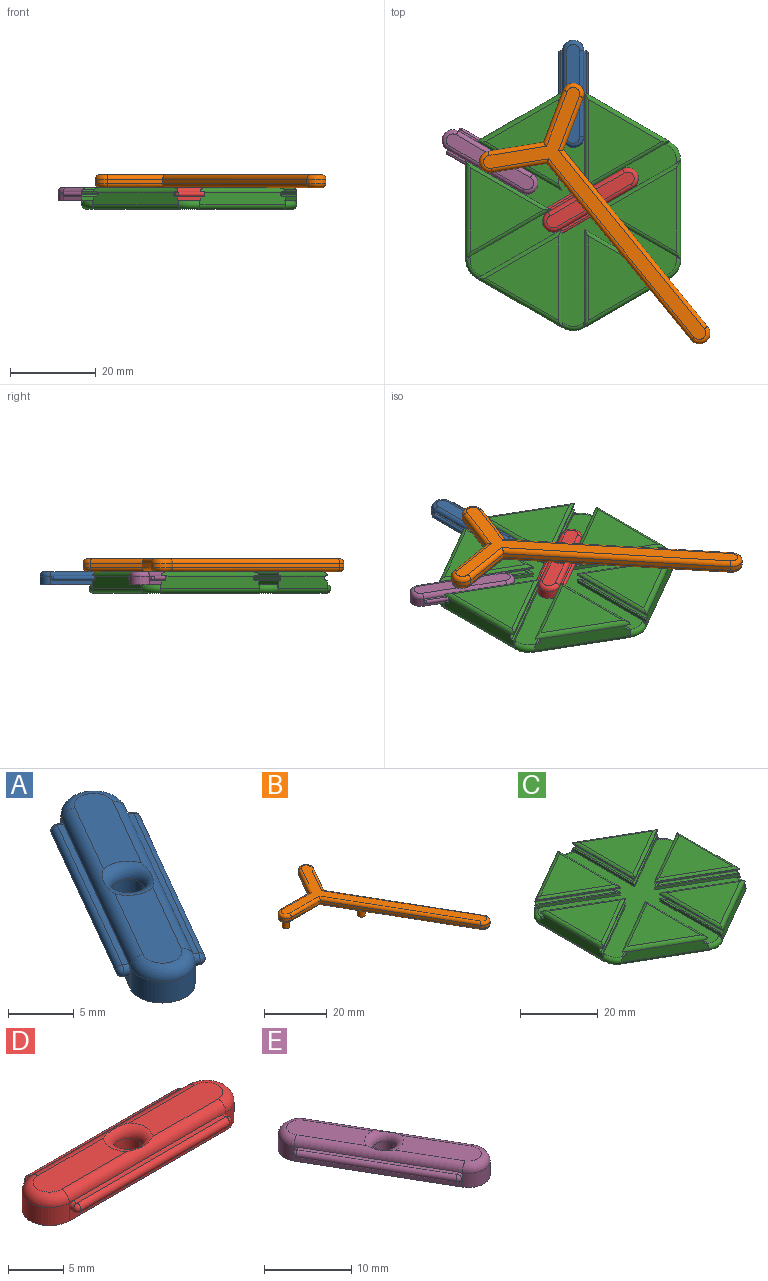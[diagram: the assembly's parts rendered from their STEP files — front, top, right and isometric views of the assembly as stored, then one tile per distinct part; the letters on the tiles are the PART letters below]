
ASSEMBLY  parts=5 mates=9
PART A: 27 faces, bbox 15.7x22.7x3 mm
  f0: plane 17.32x10mm, normal (0.87,-0.5,0), area 20.1mm2, adj f4,f5,f7,f16,f22,f25
  f1: plane 17.32x10mm, normal (-0.87,0.5,0), area 20.1mm2, adj f4,f5,f7,f14,f17,f19
  f2: plane 9.46x6.96mm, normal (0,0,1), area 27.3mm2, adj f8,f10,f11,f12
  f3: plane 9.46x6.96mm, normal (0,0,1), area 27.3mm2, adj f8,f9,f10,f12
  f4: cylinder r=2.5mm len=4.75mm, axis (0,0,-1), area 15.8mm2, adj f0,f1,f5,f8,f11,f12,f19,f25
  f5: plane 22.32x15mm, normal (0,0,-1), area 114.7mm2, adj f0,f1,f4,f6,f7
  f6: cylinder r=1.25mm len=2.5mm, axis (0,0,-1), area 15.7mm2, adj f5,f10
  f7: cylinder r=2.5mm len=4.75mm, axis (0,0,-1), area 15.8mm2, adj f0,f1,f5,f8,f9,f12,f17,f22
  f8: cylinder r=1mm len=17.82mm, axis (0.5,0.87,0), area 30.6mm2, adj f2,f3,f4,f7,f9,f10,f11,f13
  f9: torus R=1.5mm, axis (0,0,1), area 10.5mm2, adj f3,f7,f8,f12
  f10: torus R=2.25mm, axis (0,0,1), area 14.1mm2, adj f2,f3,f6,f8,f12
  f11: torus R=1.5mm, axis (0,0,1), area 10.5mm2, adj f2,f4,f8,f12
  f12: cylinder r=1mm len=17.82mm, axis (-0.5,-0.87,0), area 30.6mm2, adj f2,f3,f4,f7,f9,f10,f11,f15
  f13: plane 16.71x9.93mm, normal (0,0,1), area 9.5mm2, adj f8,f17,f19,f20
  f14: plane 16.71x9.93mm, normal (0,0,-1), area 9.5mm2, adj f1,f17,f19,f20
  f15: plane 16.71x9.93mm, normal (0,0,1), area 9.5mm2, adj f12,f22,f24,f25
  f16: plane 16.71x9.93mm, normal (0,0,-1), area 9.5mm2, adj f0,f22,f24,f25
  f17: cylinder r=0.5mm len=1mm, axis (-0.87,0.5,0), area 0.8mm2, adj f1,f7,f8,f13,f14,f18
  f18: sphere r=0.5mm, area 0.8mm2, adj f17,f20
  f19: cylinder r=0.5mm len=1mm, axis (0.87,-0.5,0), area 0.8mm2, adj f1,f4,f8,f13,f14,f21
  f20: cylinder r=0.5mm len=16.71mm, axis (0.5,0.87,0), area 29.8mm2, adj f13,f14,f18,f21
  f21: sphere r=0.5mm, area 0.8mm2, adj f19,f20
  f22: cylinder r=0.5mm len=1mm, axis (-0.87,0.5,0), area 0.8mm2, adj f0,f7,f12,f15,f16,f23
  f23: sphere r=0.5mm, area 0.8mm2, adj f22,f24
  f24: cylinder r=0.5mm len=16.71mm, axis (-0.5,-0.87,0), area 29.8mm2, adj f15,f16,f23,f26
  f25: cylinder r=0.5mm len=1mm, axis (0.87,-0.5,0), area 0.8mm2, adj f0,f4,f12,f15,f16,f26
  f26: sphere r=0.5mm, area 0.8mm2, adj f24,f25
PART B: 35 faces, bbox 47.1x65.1x6 mm
  f0: cylinder r=2.5mm len=5mm, axis (0,0,-1), area 7.9mm2, adj f1,f8,f11,f29
  f1: plane 12.99x1mm, normal (0,-1,0), area 13mm2, adj f0,f2,f13,f27
  f2: plane 45.89x26.5mm, normal (-0.87,-0.5,0), area 53mm2, adj f1,f3,f15,f26
  f3: cylinder r=2.5mm len=4.67mm, axis (0,0,-1), area 7.9mm2, adj f2,f4,f17,f28
  f4: plane 45.89x26.5mm, normal (0.87,0.5,0), area 53mm2, adj f3,f5,f19,f30
  f5: plane 11.25x6.5mm, normal (0.87,-0.5,0), area 13mm2, adj f4,f6,f18,f32
  f6: cylinder r=2.5mm len=4.67mm, axis (0,0,-1), area 7.9mm2, adj f5,f7,f16,f34
  f7: plane 11.25x6.5mm, normal (-0.87,0.5,0), area 13mm2, adj f6,f8,f14,f33
  f8: plane 12.99x1mm, normal (0,1,0), area 13mm2, adj f0,f7,f12,f31
  f9: plane 62.64x44.65mm, normal (0,0,1), area 256.6mm2, adj f11,f12,f13,f14,f15,f16,f17,f18
  f10: plane 62.64x44.65mm, normal (0,0,-1), area 243.6mm2, adj f20,f22,f24,f26,f27,f28,f29,f30
  f11: torus R=1.5mm, axis (0,0,1), area 10.5mm2, adj f0,f9,f12,f13
  f12: cylinder r=1mm len=13.57mm, axis (1,0,0), area 20.7mm2, adj f8,f9,f11,f14
  f13: cylinder r=1mm len=13.57mm, axis (-1,0,0), area 20.7mm2, adj f1,f9,f11,f15
  f14: cylinder r=1mm len=12.25mm, axis (0.5,0.87,0), area 20.7mm2, adj f7,f9,f12,f16
  f15: cylinder r=1mm len=46.89mm, axis (-0.5,0.87,0), area 83.6mm2, adj f2,f9,f13,f17
  f16: torus R=1.5mm, axis (0,0,1), area 10.5mm2, adj f6,f9,f14,f18
  f17: torus R=1.5mm, axis (0,0,1), area 10.5mm2, adj f3,f9,f15,f19
  f18: cylinder r=1mm len=12.25mm, axis (-0.5,-0.87,0), area 20.7mm2, adj f5,f9,f16,f19
  f19: cylinder r=1mm len=46.89mm, axis (0.5,-0.87,0), area 83.6mm2, adj f4,f9,f17,f18
  f20: cylinder r=1.18mm len=3mm, axis (0,0,1), area 22.1mm2, adj f10,f21
  f21: plane 2.35x2.35mm, normal (0,0,-1), area 4.3mm2, adj f20
  f22: cylinder r=1.18mm len=3mm, axis (0,0,1), area 22.1mm2, adj f10,f23
  f23: plane 2.35x2.35mm, normal (0,0,-1), area 4.3mm2, adj f22
  f24: cylinder r=1.18mm len=3mm, axis (0,0,1), area 22.1mm2, adj f10,f25
  f25: plane 2.35x2.35mm, normal (0,0,-1), area 4.3mm2, adj f24
  f26: cylinder r=1mm len=46.89mm, axis (0.5,-0.87,0), area 83.6mm2, adj f2,f10,f27,f28
  f27: cylinder r=1mm len=13.57mm, axis (1,0,0), area 20.7mm2, adj f1,f10,f26,f29
  f28: torus R=1.5mm, axis (0,0,1), area 10.5mm2, adj f3,f10,f26,f30
  f29: torus R=1.5mm, axis (0,0,1), area 10.5mm2, adj f0,f10,f27,f31
  f30: cylinder r=1mm len=46.89mm, axis (-0.5,0.87,0), area 83.6mm2, adj f4,f10,f28,f32
  f31: cylinder r=1mm len=13.57mm, axis (-1,0,0), area 20.7mm2, adj f8,f10,f29,f33
  f32: cylinder r=1mm len=12.25mm, axis (0.5,0.87,0), area 20.7mm2, adj f5,f10,f30,f34
  f33: cylinder r=1mm len=12.25mm, axis (-0.5,-0.87,0), area 20.7mm2, adj f7,f10,f31,f34
  f34: torus R=1.5mm, axis (0,0,1), area 10.5mm2, adj f6,f10,f32,f33
PART C: 126 faces, bbox 50.8x57x5 mm
  f0: cylinder r=1mm len=20.19mm, axis (0.87,-0.5,0), area 33.9mm2, adj f6,f36,f47,f50,f78,f79,f81,f123
  f1: cylinder r=1mm len=20.19mm, axis (0.87,0.5,0), area 33.9mm2, adj f7,f37,f48,f51,f76,f77,f85,f121
  f2: cylinder r=1mm len=22.73mm, axis (0,1,0), area 33.9mm2, adj f8,f38,f49,f52,f74,f75,f89,f119
  f3: cylinder r=1mm len=20.19mm, axis (-0.87,0.5,0), area 33.9mm2, adj f9,f39,f44,f53,f72,f73,f93,f117
  f4: cylinder r=1mm len=20.19mm, axis (-0.87,-0.5,0), area 33.9mm2, adj f10,f40,f45,f54,f70,f71,f97,f115
  f5: cylinder r=1mm len=22.73mm, axis (0,-1,0), area 33.9mm2, adj f11,f41,f46,f55,f68,f69,f100,f102
  f6: plane 20x11.55mm, normal (-0.5,-0.87,0), area 66.1mm2, adj f0,f22,f23,f30,f31,f42,f59,f80
  f7: plane 20x11.55mm, normal (0.5,-0.87,0), area 66.1mm2, adj f1,f20,f21,f32,f33,f42,f63,f84
  f8: plane 23.09x3mm, normal (1,0,0), area 66.1mm2, adj f2,f18,f19,f34,f35,f42,f66,f88
  f9: plane 20x11.55mm, normal (0.5,0.87,0), area 66.1mm2, adj f3,f16,f17,f24,f25,f42,f65,f92
  f10: plane 20x11.55mm, normal (-0.5,0.87,0), area 66.1mm2, adj f4,f14,f15,f26,f27,f42,f62,f96
  f11: plane 23.09x3mm, normal (-1,0,0), area 66mm2, adj f5,f12,f13,f28,f29,f42,f58,f101
  f12: plane 19.7x11.37mm, normal (0.5,0.87,0), area 19.3mm2, adj f11,f13,f42,f101
  f13: plane 19.7x11.37mm, normal (0.5,-0.87,0), area 19.3mm2, adj f11,f12,f42,f101
  f14: plane 22.75x0.85mm, normal (1,0,0), area 19.3mm2, adj f10,f15,f42,f96
  f15: plane 19.7x11.37mm, normal (-0.5,-0.87,0), area 19.3mm2, adj f10,f14,f42,f96
  f16: plane 19.7x11.37mm, normal (0.5,-0.87,0), area 19.3mm2, adj f9,f17,f42,f92
  f17: plane 22.75x0.85mm, normal (-1,0,0), area 19.3mm2, adj f9,f16,f42,f92
  f18: plane 19.7x11.37mm, normal (-0.5,-0.87,0), area 19.3mm2, adj f8,f19,f42,f88
  f19: plane 19.7x11.37mm, normal (-0.5,0.87,0), area 19.3mm2, adj f8,f18,f42,f88
  f20: plane 22.75x0.85mm, normal (-1,0,0), area 19.3mm2, adj f7,f21,f42,f84
  f21: plane 19.7x11.37mm, normal (0.5,0.87,0), area 19.3mm2, adj f7,f20,f42,f84
  f22: plane 19.7x11.37mm, normal (-0.5,0.87,0), area 19.3mm2, adj f6,f23,f42,f80
  f23: plane 22.75x0.85mm, normal (1,0,0), area 19.3mm2, adj f6,f22,f42,f80
  f24: plane 1.05x1mm, normal (0.5,-0.87,0), area 0.3mm2, adj f9,f42,f67
  f25: plane 1.21x1mm, normal (-1,0,0), area 0.3mm2, adj f9,f42,f61
  f26: plane 1.21x1mm, normal (1,0,0), area 0.3mm2, adj f10,f42,f61
  f27: plane 1.05x1mm, normal (-0.5,-0.87,0), area 0.3mm2, adj f10,f42,f57
  f28: plane 1.05x1mm, normal (0.5,0.87,0), area 0.3mm2, adj f11,f42,f57
  f29: plane 1.05x1mm, normal (0.5,-0.87,0), area 0.3mm2, adj f11,f42,f56
  f30: plane 1.05x1mm, normal (-0.5,0.87,0), area 0.3mm2, adj f6,f42,f56
  f31: plane 1.21x1mm, normal (1,0,0), area 0.3mm2, adj f6,f42,f60
  f32: plane 1.21x1mm, normal (-1,0,0), area 0.3mm2, adj f7,f42,f60
  f33: plane 1.05x1mm, normal (0.5,0.87,0), area 0.3mm2, adj f7,f42,f64
  f34: plane 1.05x1mm, normal (-0.5,-0.87,0), area 0.3mm2, adj f8,f42,f64
  f35: plane 1.05x1mm, normal (-0.5,0.87,0), area 0.3mm2, adj f8,f42,f67
  f36: cylinder r=1mm len=19.98mm, axis (0.87,0.5,0), area 21.6mm2, adj f0,f47,f50,f78
  f37: cylinder r=1mm len=22.57mm, axis (0,1,0), area 21.6mm2, adj f1,f48,f51,f76
  f38: cylinder r=1mm len=19.98mm, axis (-0.87,0.5,0), area 21.6mm2, adj f2,f49,f52,f74
  f39: cylinder r=1mm len=19.98mm, axis (-0.87,-0.5,0), area 21.6mm2, adj f3,f44,f53,f72
  f40: cylinder r=1mm len=22.57mm, axis (0,-1,0), area 21.6mm2, adj f4,f45,f54,f70
  f41: cylinder r=1mm len=19.98mm, axis (0.87,-0.5,0), area 21.6mm2, adj f5,f46,f55,f68
  f42: plane 54.85x50mm, normal (0,0,1), area 780.8mm2, adj f6,f7,f8,f9,f10,f11,f12,f13
  f43: plane 54.19x48mm, normal (0,0,-1), area 1990.2mm2, adj f56,f57,f58,f59,f60,f61,f62,f63
  f44: plane 19.63x17mm, normal (0,0,1), area 166.9mm2, adj f3,f39,f53
  f45: plane 19.63x17mm, normal (0,0,1), area 166.9mm2, adj f4,f40,f54
  f46: plane 19.63x17mm, normal (0,0,1), area 166.9mm2, adj f5,f41,f55
  f47: plane 19.63x17mm, normal (0,0,1), area 166.9mm2, adj f0,f36,f50
  f48: plane 19.63x17mm, normal (0,0,1), area 166.9mm2, adj f1,f37,f51
  f49: plane 19.63x17mm, normal (0,0,1), area 166.9mm2, adj f2,f38,f52
  f50: cylinder r=1mm len=22.57mm, axis (0,-1,0), area 21.6mm2, adj f0,f36,f47,f79
  f51: cylinder r=1mm len=19.98mm, axis (0.87,-0.5,0), area 21.6mm2, adj f1,f37,f48,f77
  f52: cylinder r=1mm len=19.98mm, axis (0.87,0.5,0), area 21.6mm2, adj f2,f38,f49,f75
  f53: cylinder r=1mm len=22.57mm, axis (0,1,0), area 21.6mm2, adj f3,f39,f44,f73
  f54: cylinder r=1mm len=19.98mm, axis (-0.87,0.5,0), area 21.6mm2, adj f4,f40,f45,f71
  f55: cylinder r=1mm len=19.98mm, axis (-0.87,-0.5,0), area 21.6mm2, adj f5,f41,f46,f69
  f56: torus R=4mm, axis (0,0,1), area 15.9mm2, adj f29,f30,f42,f43,f58,f59
  f57: torus R=4mm, axis (0,0,1), area 15.9mm2, adj f27,f28,f42,f43,f58,f62
  f58: cylinder r=1mm len=23.09mm, axis (0,1,0), area 36.3mm2, adj f11,f43,f56,f57
  f59: cylinder r=1mm len=20.5mm, axis (-0.87,0.5,0), area 36.3mm2, adj f6,f43,f56,f60
  f60: torus R=4mm, axis (0,0,1), area 15.9mm2, adj f31,f32,f42,f43,f59,f63
  f61: torus R=4mm, axis (0,0,1), area 15.9mm2, adj f25,f26,f42,f43,f62,f65
  f62: cylinder r=1mm len=20.5mm, axis (0.87,0.5,0), area 36.3mm2, adj f10,f43,f57,f61
  f63: cylinder r=1mm len=20.5mm, axis (-0.87,-0.5,0), area 36.3mm2, adj f7,f43,f60,f64
  f64: torus R=4mm, axis (0,0,1), area 15.9mm2, adj f33,f34,f42,f43,f63,f66
  f65: cylinder r=1mm len=20.5mm, axis (0.87,-0.5,0), area 36.3mm2, adj f9,f43,f61,f67
  f66: cylinder r=1mm len=23.09mm, axis (0,-1,0), area 36.3mm2, adj f8,f43,f64,f67
  f67: torus R=4mm, axis (0,0,1), area 15.9mm2, adj f24,f35,f42,f43,f65,f66
  f68: plane 19.71x11.39mm, normal (0.5,0.87,0), area 8.5mm2, adj f5,f41,f69,f100
  f69: plane 19.71x11.39mm, normal (0.5,-0.87,0), area 8.5mm2, adj f5,f55,f68,f100
  f70: plane 22.76x0.4mm, normal (1,0,0), area 8.5mm2, adj f4,f40,f71,f97
  f71: plane 19.71x11.39mm, normal (-0.5,-0.87,0), area 8.5mm2, adj f4,f54,f70,f97
  f72: plane 19.71x11.39mm, normal (0.5,-0.87,0), area 8.5mm2, adj f3,f39,f73,f93
  f73: plane 22.76x0.4mm, normal (-1,0,0), area 8.5mm2, adj f3,f53,f72,f93
  f74: plane 19.71x11.39mm, normal (-0.5,-0.87,0), area 8.5mm2, adj f2,f38,f75,f89
  f75: plane 19.71x11.39mm, normal (-0.5,0.87,0), area 8.5mm2, adj f2,f52,f74,f89
  f76: plane 22.76x0.4mm, normal (-1,0,0), area 8.5mm2, adj f1,f37,f77,f85
  f77: plane 19.71x11.39mm, normal (0.5,0.87,0), area 8.5mm2, adj f1,f51,f76,f85
  f78: plane 19.71x11.39mm, normal (-0.5,0.87,0), area 8.5mm2, adj f0,f36,f79,f81
  f79: plane 22.76x0.4mm, normal (1,0,0), area 8.5mm2, adj f0,f50,f78,f81
  f80: plane 22.75x19.7mm, normal (0,0,1), area 22.2mm2, adj f6,f22,f23,f112,f113
  f81: plane 22.73x19.69mm, normal (0,0,-1), area 22.2mm2, adj f0,f78,f79,f123,f124
  f82: plane 20.44x0.3mm, normal (1,0,0), area 6.1mm2, adj f6,f83,f113,f124
  f83: plane 17.7x10.22mm, normal (-0.5,0.87,0), area 6.1mm2, adj f6,f82,f112,f123
  f84: plane 22.75x19.7mm, normal (0,0,1), area 22.2mm2, adj f7,f20,f21,f110,f111
  f85: plane 22.73x19.69mm, normal (0,0,-1), area 22.2mm2, adj f1,f76,f77,f121,f122
  f86: plane 17.7x10.22mm, normal (0.5,0.87,0), area 6.1mm2, adj f7,f87,f111,f122
  f87: plane 20.44x0.3mm, normal (-1,0,0), area 6.1mm2, adj f7,f86,f110,f121
  f88: plane 22.75x19.7mm, normal (0,0,1), area 22.2mm2, adj f8,f18,f19,f108,f109
  f89: plane 22.73x19.69mm, normal (0,0,-1), area 22.2mm2, adj f2,f74,f75,f119,f120
  f90: plane 17.7x10.22mm, normal (-0.5,0.87,0), area 6.1mm2, adj f8,f91,f109,f120
  f91: plane 17.7x10.22mm, normal (-0.5,-0.87,0), area 6.1mm2, adj f8,f90,f108,f119
  f92: plane 22.75x19.7mm, normal (0,0,1), area 22.2mm2, adj f9,f16,f17,f106,f107
  f93: plane 22.73x19.69mm, normal (0,0,-1), area 22.2mm2, adj f3,f72,f73,f117,f118
  f94: plane 20.44x0.3mm, normal (-1,0,0), area 6.1mm2, adj f9,f95,f107,f118
  f95: plane 17.7x10.22mm, normal (0.5,-0.87,0), area 6.1mm2, adj f9,f94,f106,f117
  f96: plane 22.75x19.7mm, normal (0,0,1), area 22.2mm2, adj f10,f14,f15,f104,f105
  f97: plane 22.73x19.69mm, normal (0,0,-1), area 22.2mm2, adj f4,f70,f71,f115,f116
  f98: plane 17.7x10.22mm, normal (-0.5,-0.87,0), area 6.1mm2, adj f10,f99,f105,f116
  f99: plane 20.44x0.3mm, normal (1,0,0), area 6.1mm2, adj f10,f98,f104,f115
  f100: plane 22.73x19.69mm, normal (0,0,-1), area 32.8mm2, adj f5,f68,f69,f102,f125
  f101: plane 22.75x19.7mm, normal (0,0,1), area 32.8mm2, adj f11,f12,f13,f102,f114
  f102: plane 18.2x10.51mm, normal (0.5,0.87,0), area 26.7mm2, adj f5,f11,f100,f101,f103,f114,f125
  f103: plane 17.7x10.22mm, normal (0.5,-0.87,0), area 6.1mm2, adj f11,f102,f114,f125
  f104: cylinder r=0.5mm len=21.59mm, axis (0,1,0), area 16.4mm2, adj f10,f96,f99,f105
  f105: cylinder r=0.5mm len=18.95mm, axis (0.87,-0.5,0), area 16.4mm2, adj f10,f96,f98,f104
  f106: cylinder r=0.5mm len=18.95mm, axis (0.87,0.5,0), area 16.4mm2, adj f9,f92,f95,f107
  f107: cylinder r=0.5mm len=21.59mm, axis (0,-1,0), area 16.4mm2, adj f9,f92,f94,f106
  f108: cylinder r=0.5mm len=18.95mm, axis (0.87,-0.5,0), area 16.4mm2, adj f8,f88,f91,f109
  f109: cylinder r=0.5mm len=18.95mm, axis (-0.87,-0.5,0), area 16.4mm2, adj f8,f88,f90,f108
  f110: cylinder r=0.5mm len=21.59mm, axis (0,-1,0), area 16.4mm2, adj f7,f84,f87,f111
  f111: cylinder r=0.5mm len=18.95mm, axis (-0.87,0.5,0), area 16.4mm2, adj f7,f84,f86,f110
  f112: cylinder r=0.5mm len=18.95mm, axis (-0.87,-0.5,0), area 16.4mm2, adj f6,f80,f83,f113
  f113: cylinder r=0.5mm len=21.59mm, axis (0,1,0), area 16.4mm2, adj f6,f80,f82,f112
  f114: cylinder r=0.5mm len=18.45mm, axis (0.87,0.5,0), area 16.2mm2, adj f11,f101,f102,f103
  f115: cylinder r=0.5mm len=21.58mm, axis (0,-1,0), area 16.4mm2, adj f4,f10,f97,f99,f116
  f116: cylinder r=0.5mm len=18.94mm, axis (-0.87,0.5,0), area 16.4mm2, adj f4,f10,f97,f98,f115
  f117: cylinder r=0.5mm len=18.94mm, axis (-0.87,-0.5,0), area 16.4mm2, adj f3,f9,f93,f95,f118
  f118: cylinder r=0.5mm len=21.58mm, axis (0,1,0), area 16.4mm2, adj f3,f9,f93,f94,f117
  f119: cylinder r=0.5mm len=18.94mm, axis (-0.87,0.5,0), area 16.4mm2, adj f2,f8,f89,f91,f120
  f120: cylinder r=0.5mm len=18.94mm, axis (0.87,0.5,0), area 16.4mm2, adj f2,f8,f89,f90,f119
  f121: cylinder r=0.5mm len=21.58mm, axis (0,1,0), area 16.4mm2, adj f1,f7,f85,f87,f122
  f122: cylinder r=0.5mm len=18.94mm, axis (0.87,-0.5,0), area 16.4mm2, adj f1,f7,f85,f86,f121
  f123: cylinder r=0.5mm len=18.94mm, axis (0.87,0.5,0), area 16.4mm2, adj f0,f6,f81,f83,f124
  f124: cylinder r=0.5mm len=21.58mm, axis (0,-1,0), area 16.4mm2, adj f0,f6,f81,f82,f123
  f125: cylinder r=0.5mm len=18.44mm, axis (-0.87,-0.5,0), area 16.2mm2, adj f5,f11,f100,f102,f103
PART D: 27 faces, bbox 25.4x7x3 mm
  f0: plane 20x1.5mm, normal (0,1,0), area 20.1mm2, adj f4,f5,f7,f16,f17,f19
  f1: plane 20x1.5mm, normal (0,-1,0), area 20.1mm2, adj f4,f5,f7,f14,f22,f25
  f2: plane 9.82x3mm, normal (0,0,1), area 27.3mm2, adj f8,f10,f11,f12
  f3: plane 9.82x3mm, normal (0,0,1), area 27.3mm2, adj f8,f9,f10,f12
  f4: cylinder r=2.5mm len=5mm, axis (0,0,-1), area 15.8mm2, adj f0,f1,f5,f8,f11,f12,f17,f22
  f5: plane 25x5.01mm, normal (0,0,-1), area 114.7mm2, adj f0,f1,f4,f6,f7
  f6: cylinder r=1.25mm len=2.5mm, axis (0,0,-1), area 15.7mm2, adj f5,f10
  f7: cylinder r=2.5mm len=5mm, axis (0,0,-1), area 15.8mm2, adj f0,f1,f5,f8,f9,f12,f19,f25
  f8: cylinder r=1mm len=20mm, axis (-1,0,0), area 30.6mm2, adj f2,f3,f4,f7,f9,f10,f11,f13
  f9: torus R=1.5mm, axis (0,0,1), area 10.5mm2, adj f3,f7,f8,f12
  f10: torus R=2.25mm, axis (0,0,1), area 14.1mm2, adj f2,f3,f6,f8,f12
  f11: torus R=1.5mm, axis (0,0,1), area 10.5mm2, adj f2,f4,f8,f12
  f12: cylinder r=1mm len=20mm, axis (1,0,0), area 30.6mm2, adj f2,f3,f4,f7,f9,f10,f11,f15
  f13: plane 19x0.51mm, normal (0,0,1), area 9.5mm2, adj f8,f22,f24,f25
  f14: plane 19x0.51mm, normal (0,0,-1), area 9.5mm2, adj f1,f22,f24,f25
  f15: plane 19x0.51mm, normal (0,0,1), area 9.5mm2, adj f12,f17,f19,f20
  f16: plane 19x0.51mm, normal (0,0,-1), area 9.5mm2, adj f0,f17,f19,f20
  f17: cylinder r=0.5mm len=1mm, axis (0,1,0), area 0.8mm2, adj f0,f4,f12,f15,f16,f18
  f18: sphere r=0.5mm, area 0.8mm2, adj f17,f20
  f19: cylinder r=0.5mm len=1mm, axis (0,-1,0), area 0.8mm2, adj f0,f7,f12,f15,f16,f21
  f20: cylinder r=0.5mm len=19mm, axis (1,0,0), area 29.8mm2, adj f15,f16,f18,f21
  f21: sphere r=0.5mm, area 0.8mm2, adj f19,f20
  f22: cylinder r=0.5mm len=1mm, axis (0,1,0), area 0.8mm2, adj f1,f4,f8,f13,f14,f23
  f23: sphere r=0.5mm, area 0.8mm2, adj f22,f24
  f24: cylinder r=0.5mm len=19mm, axis (-1,0,0), area 29.8mm2, adj f13,f14,f23,f26
  f25: cylinder r=0.5mm len=1mm, axis (0,-1,0), area 0.8mm2, adj f1,f7,f8,f13,f14,f26
  f26: sphere r=0.5mm, area 0.8mm2, adj f24,f25
PART E: 27 faces, bbox 15.7x22.7x3 mm
  f0: plane 17.32x10mm, normal (-0.87,-0.5,0), area 20.1mm2, adj f4,f6,f7,f16,f22,f25
  f1: plane 17.32x10mm, normal (0.87,0.5,0), area 20.1mm2, adj f4,f6,f7,f14,f17,f19
  f2: plane 9.46x6.96mm, normal (0,0,1), area 27.3mm2, adj f8,f10,f11,f12
  f3: plane 9.46x6.96mm, normal (0,0,1), area 27.3mm2, adj f8,f9,f10,f11
  f4: plane 22.32x15mm, normal (0,0,-1), area 114.7mm2, adj f0,f1,f5,f6,f7
  f5: cylinder r=1.25mm len=2.5mm, axis (0,0,-1), area 15.7mm2, adj f4,f8
  f6: cylinder r=2.5mm len=4.75mm, axis (0,0,-1), area 15.8mm2, adj f0,f1,f4,f10,f11,f12,f19,f25
  f7: cylinder r=2.5mm len=4.75mm, axis (0,0,-1), area 15.8mm2, adj f0,f1,f4,f9,f10,f11,f17,f22
  f8: torus R=2.25mm, axis (0,0,1), area 14.1mm2, adj f2,f3,f5,f10,f11
  f9: torus R=1.5mm, axis (0,0,1), area 10.5mm2, adj f3,f7,f10,f11
  f10: cylinder r=1mm len=17.82mm, axis (-0.5,0.87,0), area 30.6mm2, adj f2,f3,f6,f7,f8,f9,f12,f15
  f11: cylinder r=1mm len=17.82mm, axis (0.5,-0.87,0), area 30.6mm2, adj f2,f3,f6,f7,f8,f9,f12,f13
  f12: torus R=1.5mm, axis (0,0,1), area 10.5mm2, adj f2,f6,f10,f11
  f13: plane 16.7x9.94mm, normal (0,0,1), area 9.5mm2, adj f11,f17,f19,f20
  f14: plane 16.7x9.94mm, normal (0,0,-1), area 9.5mm2, adj f1,f17,f19,f20
  f15: plane 16.7x9.94mm, normal (0,0,1), area 9.5mm2, adj f10,f22,f24,f25
  f16: plane 16.7x9.94mm, normal (0,0,-1), area 9.5mm2, adj f0,f22,f24,f25
  f17: cylinder r=0.5mm len=1mm, axis (0.87,0.5,0), area 0.8mm2, adj f1,f7,f11,f13,f14,f18
  f18: sphere r=0.5mm, area 0.8mm2, adj f17,f20
  f19: cylinder r=0.5mm len=1mm, axis (-0.87,-0.5,0), area 0.8mm2, adj f1,f6,f11,f13,f14,f21
  f20: cylinder r=0.5mm len=16.7mm, axis (0.5,-0.87,0), area 29.8mm2, adj f13,f14,f18,f21
  f21: sphere r=0.5mm, area 0.8mm2, adj f19,f20
  f22: cylinder r=0.5mm len=1mm, axis (0.87,0.5,0), area 0.8mm2, adj f0,f7,f10,f15,f16,f23
  f23: sphere r=0.5mm, area 0.8mm2, adj f22,f24
  f24: cylinder r=0.5mm len=16.7mm, axis (-0.5,0.87,0), area 29.8mm2, adj f15,f16,f23,f26
  f25: cylinder r=0.5mm len=1mm, axis (-0.87,-0.5,0), area 0.8mm2, adj f0,f6,f10,f15,f16,f26
  f26: sphere r=0.5mm, area 0.8mm2, adj f24,f25
PLACE A rot(axis=(0,0,1),30deg) t=(-2.45,-2.85,1.85)mm
PLACE B rot(axis=(0,0,1),9.2deg) t=(-10.93,-5.87,1.85)mm
PLACE C t=(-14.94,-8.19,1.85)mm fixed
PLACE D rot(axis=(0,0,1),30deg) t=(14.07,-5.88,1.85)mm
PLACE E rot(axis=(0,0,-1),150deg) t=(-34.31,2.99,1.85)mm
MATE pin_slot A.f4 <-> C.f61  axis (0,0,-1) through (-14.94,28.81,1.85)mm
MATE revolute E.f5 <-> B.f0  axis (0,0,1) through (-34.31,2.99,4.85)mm
MATE revolute D.f6 <-> B.f24  axis (0,0,1) through (-10.93,-5.87,4.85)mm
MATE pin_slot A.f7 <-> C.f60  axis (0,0,-1) through (-14.94,8.81,1.85)mm
MATE pin_slot E.f7 <-> C.f64  axis (0,0,-1) through (-25.65,-2.01,1.85)mm
MATE pin_slot E.f6 <-> C.f57  axis (0,0,-1) through (-42.97,7.99,1.85)mm
MATE pin_slot D.f4 <-> C.f56  axis (0,0,-1) through (-19.59,-10.87,1.85)mm
MATE pin_slot D.f7 <-> C.f67  axis (0,0,-1) through (-2.27,-0.87,1.85)mm
MATE revolute A.f6 <-> B.f22  axis (0,0,1) through (-14.94,18.81,4.85)mm
